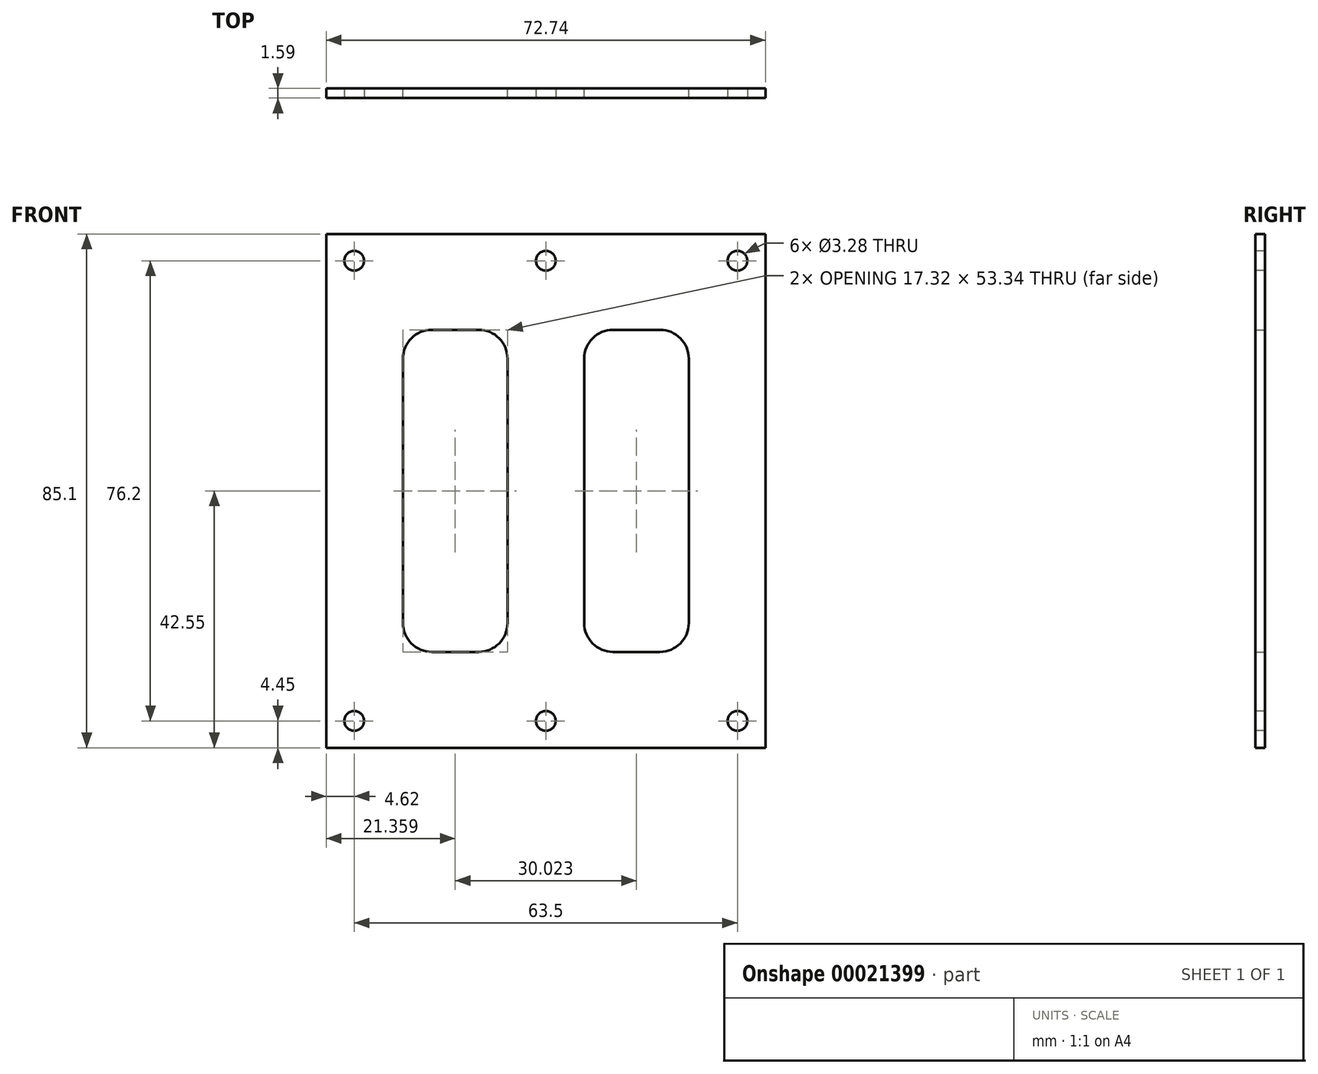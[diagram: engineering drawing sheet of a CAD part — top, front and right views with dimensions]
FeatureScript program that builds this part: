
annotation { "Feature Type Name" : "Feature", "Feature Type Description" : "" }
export const myFeature = defineFeature(function(context is Context, id is Id, definition is map)
    precondition{}
    {
        {
            var Q0;
            Q0=qCreatedBy(makeId("Front.planeOp"),FACE);
            var sketch = newSketch(context, id + "F0", { "sketchPlane" : qUnion([Q0])});
            skLineSegment(sketch, "E0.rect.bottom", {"start": v(36.37, -42.55) * mm, "end": v(-36.37, -42.55) * mm});
            skLineSegment(sketch, "E0.rect.top", {"start": v(36.37, 42.55) * mm, "end": v(-36.37, 42.54) * mm});
            skLineSegment(sketch, "E0.rect.left", {"start": v(36.37, -42.55) * mm, "end": v(36.37, 42.55) * mm});
            skLineSegment(sketch, "E0.rect.right", {"start": v(-36.37, -42.55) * mm, "end": v(-36.37, 42.54) * mm});
            skPoint(sketch, "E0.rect.middle", {"position": v(0, 0) * mm});
            skLineSegment(sketch, "E1.bottom", {"start": v(-23.67, 26.67) * mm, "end": v(-6.35, 26.67) * mm});
            skLineSegment(sketch, "E1.top", {"start": v(-23.67, -26.67) * mm, "end": v(-6.35, -26.67) * mm});
            skLineSegment(sketch, "E1.left", {"start": v(-23.67, 26.67) * mm, "end": v(-23.67, -26.67) * mm});
            skLineSegment(sketch, "E1.right", {"start": v(-6.35, 26.67) * mm, "end": v(-6.35, -26.67) * mm});
            skLineSegment(sketch, "E2.bottom", {"start": v(6.35, 26.67) * mm, "end": v(23.67, 26.67) * mm});
            skLineSegment(sketch, "E2.top", {"start": v(6.35, -26.67) * mm, "end": v(23.67, -26.67) * mm});
            skLineSegment(sketch, "E2.left", {"start": v(6.35, 26.67) * mm, "end": v(6.35, -26.67) * mm});
            skLineSegment(sketch, "E2.right", {"start": v(23.67, 26.67) * mm, "end": v(23.67, -26.67) * mm});
            skLineSegment(sketch, "E3", {"start": v(0, 0) * mm, "end": v(0, 51.32) * mm});
            skLineSegment(sketch, "E4", {"start": v(0, 0) * mm, "end": v(43.45, 0) * mm});
            skSolve(sketch);
        }
        {
            var Q0;
            {var subQ13=sQuery(id+"F0.wireOp",EDGE,"E0.rect.bottom");Q0=makeQuery(id+"F0.imprint","IMPRINT",FACE,{"disambiguationData":[TD([[makeQuery(id+"F0.imprint","IMPRINT",EDGE,{"derivedFrom":subQ13}),-1.0]])]});}
            var Q1;
            {var subQ7=sQuery(id+"F0.wireOp",EDGE,"E2.bottom");Q1=makeQuery(id+"F0.imprint","IMPRINT",FACE,{"disambiguationData":[TD([[makeQuery(id+"F0.imprint","IMPRINT",EDGE,{"derivedFrom":subQ7}),1.0]])]});}
            extrude(context, id + "F1", {"entities" : qUnion([Q0, Q1]), "depth" : 1.59 * mm});
        }
        {
            var Q0;
            Q0=makeQuery(id+"F1.opExtrude","SWEPT_EDGE",EDGE,{"disambiguationData":[OSD([sQuery(id+"F0.wireOp",EDGE,"E2.bottom"),sQuery(id+"F0.wireOp",EDGE,"E2.right")])]});
            var Q1;
            Q1=makeQuery(id+"F1.opExtrude","SWEPT_EDGE",EDGE,{"disambiguationData":[OSD([sQuery(id+"F0.wireOp",EDGE,"E2.bottom"),sQuery(id+"F0.wireOp",EDGE,"E2.left")])]});
            var Q2;
            Q2=makeQuery(id+"F1.opExtrude","SWEPT_EDGE",EDGE,{"disambiguationData":[OSD([sQuery(id+"F0.wireOp",EDGE,"E1.bottom"),sQuery(id+"F0.wireOp",EDGE,"E1.left")])]});
            var Q3;
            Q3=makeQuery(id+"F1.opExtrude","SWEPT_EDGE",EDGE,{"disambiguationData":[OSD([sQuery(id+"F0.wireOp",EDGE,"E1.bottom"),sQuery(id+"F0.wireOp",EDGE,"E1.right")])]});
            var Q4;
            Q4=makeQuery(id+"F1.opExtrude","SWEPT_EDGE",EDGE,{"disambiguationData":[OSD([sQuery(id+"F0.wireOp",EDGE,"E1.top"),sQuery(id+"F0.wireOp",EDGE,"E1.right")])]});
            var Q5;
            Q5=makeQuery(id+"F1.opExtrude","SWEPT_EDGE",EDGE,{"disambiguationData":[OSD([sQuery(id+"F0.wireOp",EDGE,"E1.top"),sQuery(id+"F0.wireOp",EDGE,"E1.left")])]});
            var Q6;
            Q6=makeQuery(id+"F1.opExtrude","SWEPT_EDGE",EDGE,{"disambiguationData":[OSD([sQuery(id+"F0.wireOp",EDGE,"E2.top"),sQuery(id+"F0.wireOp",EDGE,"E2.right")])]});
            var Q7;
            Q7=makeQuery(id+"F1.opExtrude","SWEPT_EDGE",EDGE,{"disambiguationData":[OSD([sQuery(id+"F0.wireOp",EDGE,"E2.top"),sQuery(id+"F0.wireOp",EDGE,"E2.left")])]});
            fillet(context, id + "F2", {"entities" : qUnion([Q0, Q1, Q2, Q3, Q4, Q5, Q6, Q7]), "radius" : 4.78 * mm, "tangentPropagation" : true, "allowEdgeOverflow" : false});
        }
        {
            var Q0;
            Q0=makeQuery(id+"F1.opExtrude","CAP_FACE",FACE,{"disambiguationData":[OSD([sQuery(id+"F0.wireOp",EDGE,"E0.rect.bottom"),sQuery(id+"F0.wireOp",EDGE,"E0.rect.top"),sQuery(id+"F0.wireOp",EDGE,"E0.rect.left"),sQuery(id+"F0.wireOp",EDGE,"E0.rect.right"),sQuery(id+"F0.wireOp",EDGE,"E1.bottom"),sQuery(id+"F0.wireOp",EDGE,"E1.top"),sQuery(id+"F0.wireOp",EDGE,"E1.left"),sQuery(id+"F0.wireOp",EDGE,"E1.right"),sQuery(id+"F0.wireOp",EDGE,"E2.bottom"),sQuery(id+"F0.wireOp",EDGE,"E2.top"),sQuery(id+"F0.wireOp",EDGE,"E2.left"),sQuery(id+"F0.wireOp",EDGE,"E2.right")])],"isStart":false});
            var sketch = newSketch(context, id + "F3", { "sketchPlane" : qUnion([Q0])});
            skLineSegment(sketch, "E5.rect.bottom", {"start": v(31.75, -38.1) * mm, "end": v(-31.75, -38.1) * mm});
            skLineSegment(sketch, "E5.rect.top", {"start": v(31.75, 38.1) * mm, "end": v(-31.75, 38.1) * mm});
            skLineSegment(sketch, "E5.rect.left", {"start": v(31.75, -38.1) * mm, "end": v(31.75, 38.1) * mm});
            skLineSegment(sketch, "E5.rect.right", {"start": v(-31.75, -38.1) * mm, "end": v(-31.75, 38.1) * mm});
            skPoint(sketch, "E5.rect.middle", {"position": v(0, 0) * mm});
            skLineSegment(sketch, "E6", {"start": v(0, 38.1) * mm, "end": v(0, -38.1) * mm});
            skSolve(sketch);
        }
        {
            var Q0;
            Q0=sQuery(id+"F3.wireOp",VERTEX,"E5.rect.right.end");
            var Q1;
            Q1=sQuery(id+"F3.wireOp",VERTEX,"E6.start");
            var Q2;
            Q2=sQuery(id+"F3.wireOp",VERTEX,"E5.rect.left.end");
            var Q3;
            Q3=sQuery(id+"F3.wireOp",VERTEX,"E5.rect.bottom.start");
            var Q4;
            Q4=sQuery(id+"F3.wireOp",VERTEX,"E6.end");
            var Q5;
            Q5=sQuery(id+"F3.wireOp",VERTEX,"E5.rect.right.start");
            var Q6;
            Q6=makeQuery(id+"F1.opExtrude","SWEPT_BODY",BODY,{"disambiguationData":[OSD([sQuery(id+"F0.wireOp",EDGE,"E0.rect.bottom"),sQuery(id+"F0.wireOp",EDGE,"E0.rect.top"),sQuery(id+"F0.wireOp",EDGE,"E0.rect.left"),sQuery(id+"F0.wireOp",EDGE,"E0.rect.right"),sQuery(id+"F0.wireOp",EDGE,"E1.bottom"),sQuery(id+"F0.wireOp",EDGE,"E1.top"),sQuery(id+"F0.wireOp",EDGE,"E1.left"),sQuery(id+"F0.wireOp",EDGE,"E1.right"),sQuery(id+"F0.wireOp",EDGE,"E2.bottom"),sQuery(id+"F0.wireOp",EDGE,"E2.top"),sQuery(id+"F0.wireOp",EDGE,"E2.left"),sQuery(id+"F0.wireOp",EDGE,"E2.right")])]});
            hole(context, id + "F4", {"style" : HoleStyle.SIMPLE, "holeDiameter" : 3.28 * mm, "endStyle" : HoleEndStyle.THROUGH, "locations" : qUnion([Q0, Q1, Q2, Q3, Q4, Q5]), "scope" : qUnion([Q6])});
        }
    });
